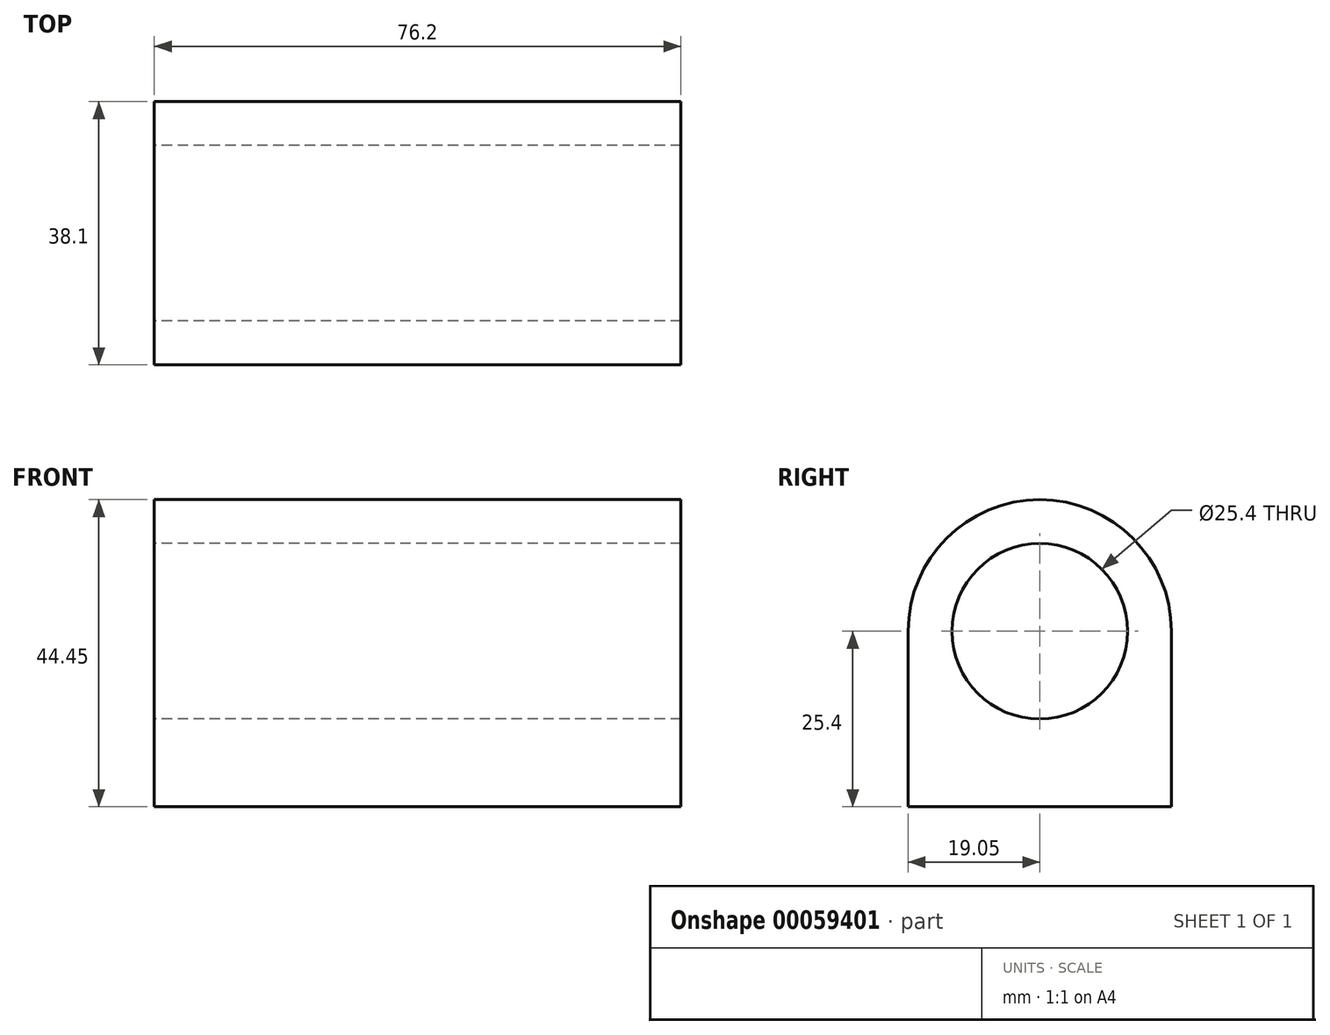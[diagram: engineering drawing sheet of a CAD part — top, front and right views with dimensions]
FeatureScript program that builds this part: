
annotation { "Feature Type Name" : "Feature", "Feature Type Description" : "" }
export const myFeature = defineFeature(function(context is Context, id is Id, definition is map)
    precondition{}
    {
        {
            var Q0;
            Q0=qCreatedBy(makeId("Right.planeOp"),FACE);
            var sketch = newSketch(context, id + "F0", { "sketchPlane" : qUnion([Q0])});
            skLineSegment(sketch, "E0", {"start": v(-19.05, 0) * mm, "end": v(-19.05, -25.4) * mm});
            skLineSegment(sketch, "E1", {"start": v(-19.05, -25.4) * mm, "end": v(19.05, -25.4) * mm});
            skLineSegment(sketch, "E2", {"start": v(19.05, -25.4) * mm, "end": v(19.05, 0) * mm});
            skArc(sketch, "E3", {"start": v(19.05, 0) * mm, "mid": v(0, 19.05) * mm, "end": v(-19.05, 0) * mm});
            skCircle(sketch, "E4", {"center": v(0, 0) * mm, "radius": 12.7 * mm});
            skSolve(sketch);
        }
        {
            var Q0;
            Q0=makeQuery(id+"F0.imprint","IMPRINT",FACE,{"disambiguationData":[TD([[makeQuery(id+"F0.imprint","IMPRINT",EDGE,{"derivedFrom":sQuery(id+"F0.wireOp",EDGE,"E0")}),1.0]])]});
            extrude(context, id + "F1", {"entities" : qUnion([Q0]), "endBound" : BoundingType.SYMMETRIC, "depth" : 76.2 * mm});
        }
    });
